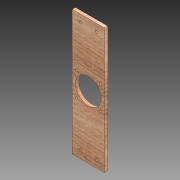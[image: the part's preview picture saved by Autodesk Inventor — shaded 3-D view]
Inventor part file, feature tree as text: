
AUTODESK INVENTOR PART (.ipt)
format: ipt  version: 2020 (Build 240168000, 168)  size: 119,808 bytes
history: native  units: mm
features: extrude x1, sketch x1
ambient origin geometry x8: Origin, YZ Plane, XZ Plane, XY Plane, X Axis, Y Axis, Z Axis, Center Point
bodies: Body1 (feature_tree)
feature tree (2):
  extrude  "Extrusion2"  Depth=100.0mm
  sketch  "Sketch1"  dims[d0=80.0mm d5=74.25mm d6=37.125mm d7=6.5mm d12=74.25mm d14=37.125mm d15=37.125mm d16=37.125mm d24=50.0mm d25=25.0mm d26=8.5mm d27=10.0mm d28=0.0mm d29=390.0mm d30=195.0mm d31=100.0mm d32=50.0mm d33=22.5mm d34=22.5mm]
